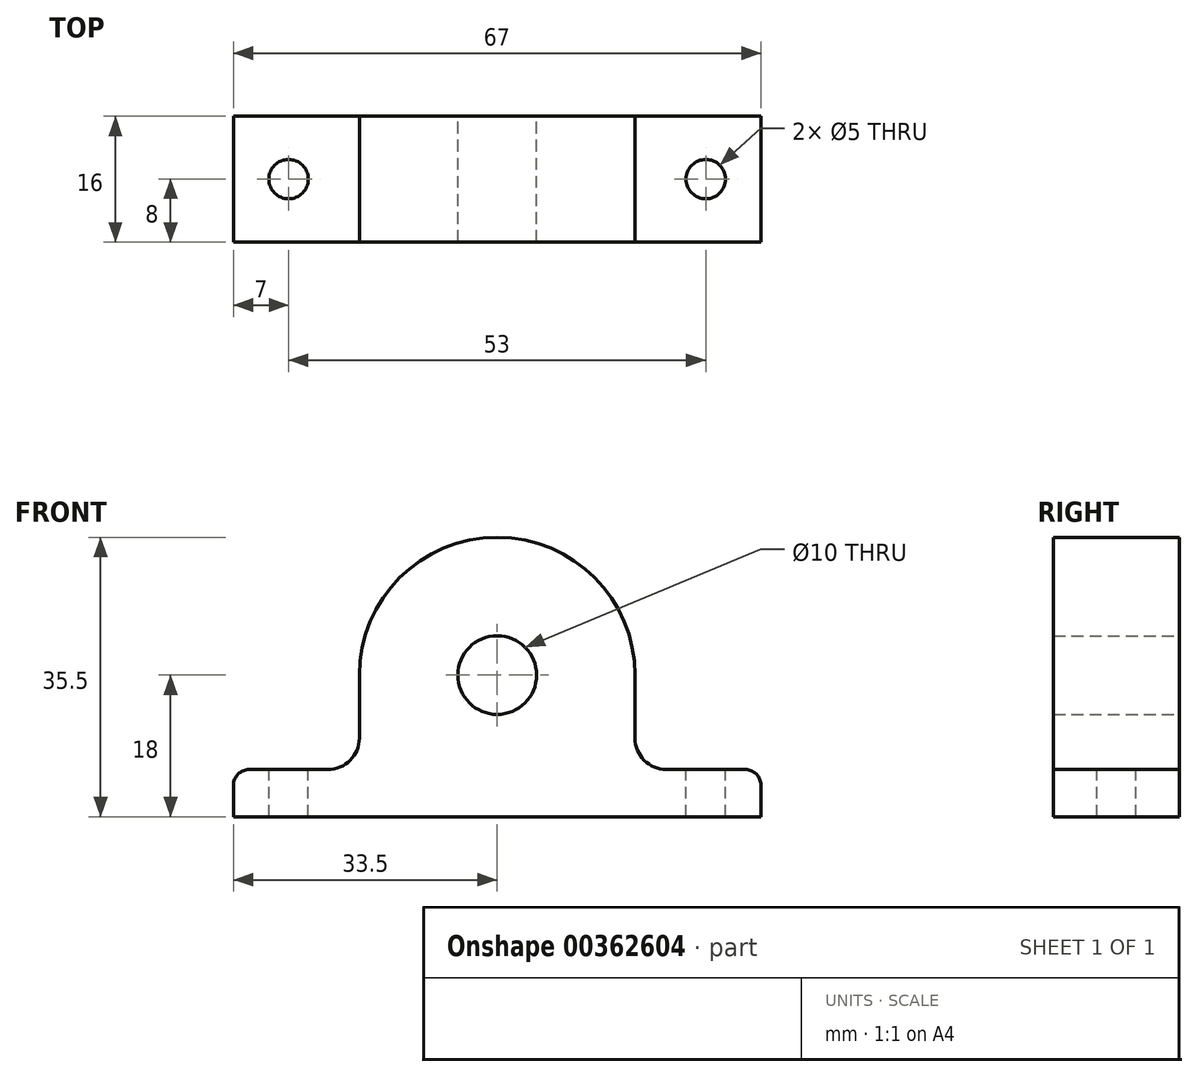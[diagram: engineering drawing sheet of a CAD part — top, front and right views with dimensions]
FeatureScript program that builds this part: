
annotation { "Feature Type Name" : "Feature", "Feature Type Description" : "" }
export const myFeature = defineFeature(function(context is Context, id is Id, definition is map)
    precondition{}
    {
        {
            var Q0;
            Q0=qCreatedBy(makeId("Front.planeOp"),FACE);
            var sketch = newSketch(context, id + "F0", { "sketchPlane" : qUnion([Q0])});
            skCircle(sketch, "E0", {"center": v(0, 0) * mm, "radius": 17.5 * mm});
            skCircle(sketch, "E1", {"center": v(0, 0) * mm, "radius": 5 * mm});
            skLineSegment(sketch, "E2.bottom", {"start": v(-31.5, -12) * mm, "end": v(-21.5, -12) * mm});
            skLineSegment(sketch, "E2.top", {"start": v(-33.5, -18) * mm, "end": v(33.5, -18) * mm});
            skLineSegment(sketch, "E2.left", {"start": v(-33.5, -14) * mm, "end": v(-33.5, -18) * mm});
            skLineSegment(sketch, "E2.right", {"start": v(33.5, -14) * mm, "end": v(33.5, -18) * mm});
            skLineSegment(sketch, "E3", {"start": v(-17.5, 0) * mm, "end": v(-17.5, -8) * mm});
            skLineSegment(sketch, "E4", {"start": v(17.5, 0) * mm, "end": v(17.5, -8) * mm});
            skLineSegment(sketch, "E5.trimOffspring", {"start": v(21.5, -12) * mm, "end": v(31.5, -12) * mm});
            skPoint(sketch, "E6.visualSharp", {"position": v(-17.5, -12) * mm});
            skArc(sketch, "E6.filletArc", {"start": v(-21.5, -12) * mm, "mid": v(-18.67, -10.83) * mm, "end": v(-17.5, -8) * mm});
            skPoint(sketch, "E7.visualSharp", {"position": v(17.5, -12) * mm});
            skArc(sketch, "E7.filletArc", {"start": v(17.5, -8) * mm, "mid": v(18.67, -10.83) * mm, "end": v(21.5, -12) * mm});
            skPoint(sketch, "E8.visualSharp", {"position": v(-33.5, -12) * mm});
            skArc(sketch, "E8.filletArc", {"start": v(-31.5, -12) * mm, "mid": v(-32.91, -12.59) * mm, "end": v(-33.5, -14) * mm});
            skPoint(sketch, "E9.visualSharp", {"position": v(33.5, -12) * mm});
            skArc(sketch, "E9.filletArc", {"start": v(33.5, -14) * mm, "mid": v(32.91, -12.59) * mm, "end": v(31.5, -12) * mm});
            skSolve(sketch);
        }
        {
            var Q0;
            Q0=makeQuery(id+"F0.imprint","IMPRINT",FACE,{"disambiguationData":[TD([[makeQuery(id+"F0.imprint","IMPRINT",EDGE,{"derivedFrom":sQuery(id+"F0.wireOp",EDGE,"E2.bottom")}),-1.0]])]});
            extrude(context, id + "F1", {"entities" : qUnion([Q0]), "endBound" : BoundingType.SYMMETRIC, "depth" : 16 * mm});
        }
        {
            var Q0;
            Q0=qCreatedBy(makeId("Front.planeOp"),FACE);
            var sketch = newSketch(context, id + "F2", { "sketchPlane" : qUnion([Q0])});
            skCircle(sketch, "E10", {"center": v(0, 0) * mm, "radius": 17.5 * mm});
            skCircle(sketch, "E11", {"center": v(0, 0) * mm, "radius": 5 * mm});
            skSolve(sketch);
        }
        {
            var Q0;
            Q0=makeQuery(id+"F2.imprint","IMPRINT",FACE,{"disambiguationData":[TD([[makeQuery(id+"F2.imprint","IMPRINT",EDGE,{"derivedFrom":sQuery(id+"F2.wireOp",EDGE,"E10")}),1.0]])]});
            extrude(context, id + "F3", {"entities" : qUnion([Q0]), "operationType" : NewBodyOperationType.ADD, "depth" : 8 * mm});
        }
        {
            var Q0;
            Q0 = qSketchRegion(id + "F2", true);
            extrude(context, id + "F4", {"entities" : qUnion([Q0]), "operationType" : NewBodyOperationType.ADD, "oppositeDirection" : true, "depth" : 8 * mm});
        }
        {
            var Q0;
            Q0=qCreatedBy(makeId("Top.planeOp"),FACE);
            var sketch = newSketch(context, id + "F5", { "sketchPlane" : qUnion([Q0])});
            skPoint(sketch, "E12", {"position": v(-26.5, 0) * mm});
            skPoint(sketch, "E13", {"position": v(26.5, 0) * mm});
            skSolve(sketch);
        }
        {
            var Q0;
            Q0=sQuery(id+"F5.wireOp",VERTEX,"E12");
            var Q1;
            Q1=sQuery(id+"F5.wireOp",VERTEX,"E13");
            var Q2;
            Q2=makeQuery(id+"F1.opExtrude","SWEPT_BODY",BODY,{"disambiguationData":[OSD([sQuery(id+"F0.wireOp",EDGE,"E0"),sQuery(id+"F0.wireOp",EDGE,"E2.bottom"),sQuery(id+"F0.wireOp",EDGE,"E2.top"),sQuery(id+"F0.wireOp",EDGE,"E2.left"),sQuery(id+"F0.wireOp",EDGE,"E2.right"),sQuery(id+"F0.wireOp",EDGE,"E3"),sQuery(id+"F0.wireOp",EDGE,"E4"),sQuery(id+"F0.wireOp",EDGE,"E5.trimOffspring"),sQuery(id+"F0.wireOp",EDGE,"E6.filletArc"),sQuery(id+"F0.wireOp",EDGE,"E7.filletArc"),sQuery(id+"F0.wireOp",EDGE,"E8.filletArc"),sQuery(id+"F0.wireOp",EDGE,"E9.filletArc")])]});
            hole(context, id + "F6", {"style" : HoleStyle.SIMPLE, "endStyle" : HoleEndStyle.THROUGH, "holeDiameter" : 5 * mm, "isTappedThrough" : true, "tappedDepth" : 12 * mm, "tapClearance" : 3, "locations" : qUnion([Q0, Q1]), "scope" : qUnion([Q2])});
        }
    });
